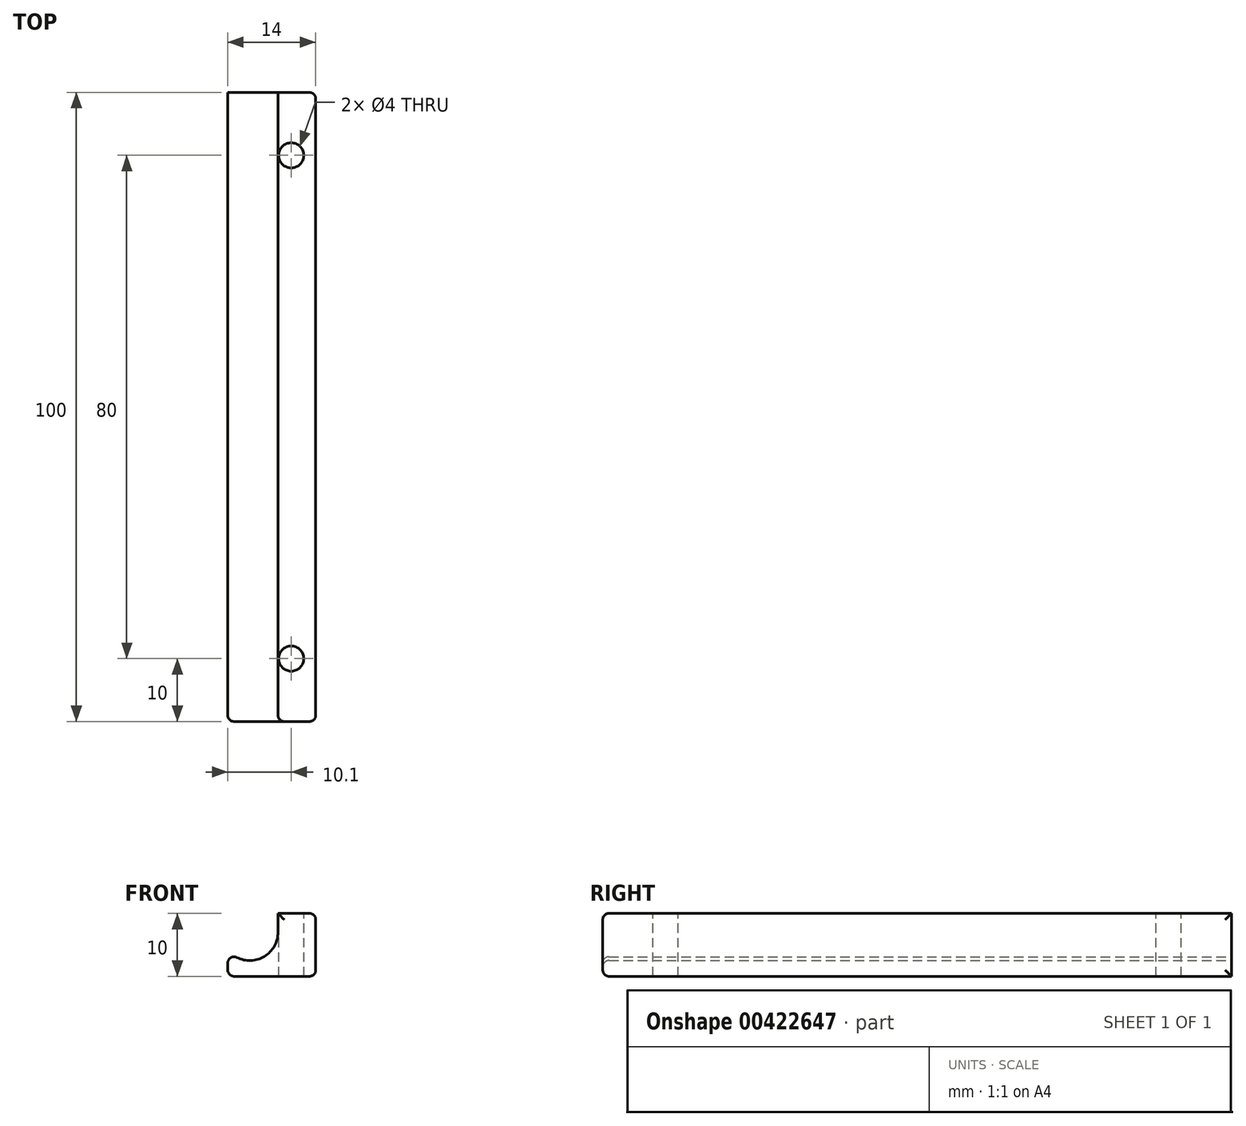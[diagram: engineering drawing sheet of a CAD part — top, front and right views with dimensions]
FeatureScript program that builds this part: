
annotation { "Feature Type Name" : "Feature", "Feature Type Description" : "" }
export const myFeature = defineFeature(function(context is Context, id is Id, definition is map)
    precondition{}
    {
        {
            var Q0;
            Q0=qCreatedBy(makeId("Front.planeOp"),FACE);
            var sketch = newSketch(context, id + "F0", { "sketchPlane" : qUnion([Q0])});
            skArc(sketch, "E0", {"start": v(-3.5, -2.83) * mm, "mid": v(1.5, -4.24) * mm, "end": v(4.5, 0) * mm});
            skLineSegment(sketch, "E1", {"start": v(4.5, 0) * mm, "end": v(4.5, 3) * mm});
            skLineSegment(sketch, "E2", {"start": v(4.5, 3) * mm, "end": v(10.5, 3) * mm});
            skLineSegment(sketch, "E3", {"start": v(10.5, 3) * mm, "end": v(10.5, -7) * mm});
            skLineSegment(sketch, "E4", {"start": v(10.5, -7) * mm, "end": v(-3.5, -7) * mm});
            skLineSegment(sketch, "E5", {"start": v(-3.5, -7) * mm, "end": v(-3.5, -2.83) * mm});
            skSolve(sketch);
        }
        {
            var Q0;
            Q0 = qSketchRegion(id + "F0", true);
            extrude(context, id + "F1", {"entities" : qUnion([Q0]), "endBound" : BoundingType.SYMMETRIC, "depth" : 100 * mm});
        }
        {
            var Q0;
            Q0=makeQuery(id+"F1.opExtrude","SWEPT_FACE",FACE,{"disambiguationData":[OSD([sQuery(id+"F0.wireOp",EDGE,"E2")])]});
            var sketch = newSketch(context, id + "F2", { "sketchPlane" : qUnion([Q0])});
            skCircle(sketch, "E6", {"center": v(6.6, -40) * mm, "radius": 2 * mm});
            skPoint(sketch, "E6.first.point", {"position": v(4.6, -40) * mm});
            skPoint(sketch, "E6.second.point", {"position": v(5.94, -41.89) * mm});
            skPoint(sketch, "E6.third.point", {"position": v(5.43, -38.38) * mm});
            skCircle(sketch, "E7", {"center": v(6.6, 40) * mm, "radius": 2 * mm});
            skSolve(sketch);
        }
        {
            var Q0;
            Q0 = qSketchRegion(id + "F2", true);
            extrude(context, id + "F3", {"entities" : qUnion([Q0]), "operationType" : NewBodyOperationType.REMOVE, "endBound" : BoundingType.UP_TO_NEXT, "oppositeDirection" : true, "depth" : 25 * mm});
        }
        {
            var Q0;
            Q0=makeQuery(id+"F1.opExtrude","SWEPT_FACE",FACE,{"disambiguationData":[OSD([sQuery(id+"F0.wireOp",EDGE,"E3")])]});
            var Q1;
            Q1=makeQuery(id+"F1.opExtrude","CAP_FACE",FACE,{"disambiguationData":[OSD([sQuery(id+"F0.wireOp",EDGE,"E0"),sQuery(id+"F0.wireOp",EDGE,"E1"),sQuery(id+"F0.wireOp",EDGE,"E2"),sQuery(id+"F0.wireOp",EDGE,"E3"),sQuery(id+"F0.wireOp",EDGE,"E4"),sQuery(id+"F0.wireOp",EDGE,"E5")])],"isStart":false});
            var Q2;
            Q2=makeQuery(id+"F1.opExtrude","SWEPT_EDGE",EDGE,{"disambiguationData":[OSD([sQuery(id+"F0.wireOp",EDGE,"E0"),sQuery(id+"F0.wireOp",EDGE,"E5")])]});
            var Q3;
            Q3=makeQuery(id+"F1.opExtrude","SWEPT_EDGE",EDGE,{"disambiguationData":[OSD([sQuery(id+"F0.wireOp",EDGE,"E4"),sQuery(id+"F0.wireOp",EDGE,"E5")])]});
            fillet(context, id + "F4", {"entities" : qUnion([Q0, Q1, Q2, Q3]), "radius" : 1 * mm, "tangentPropagation" : true, "allowEdgeOverflow" : false});
        }
    });
